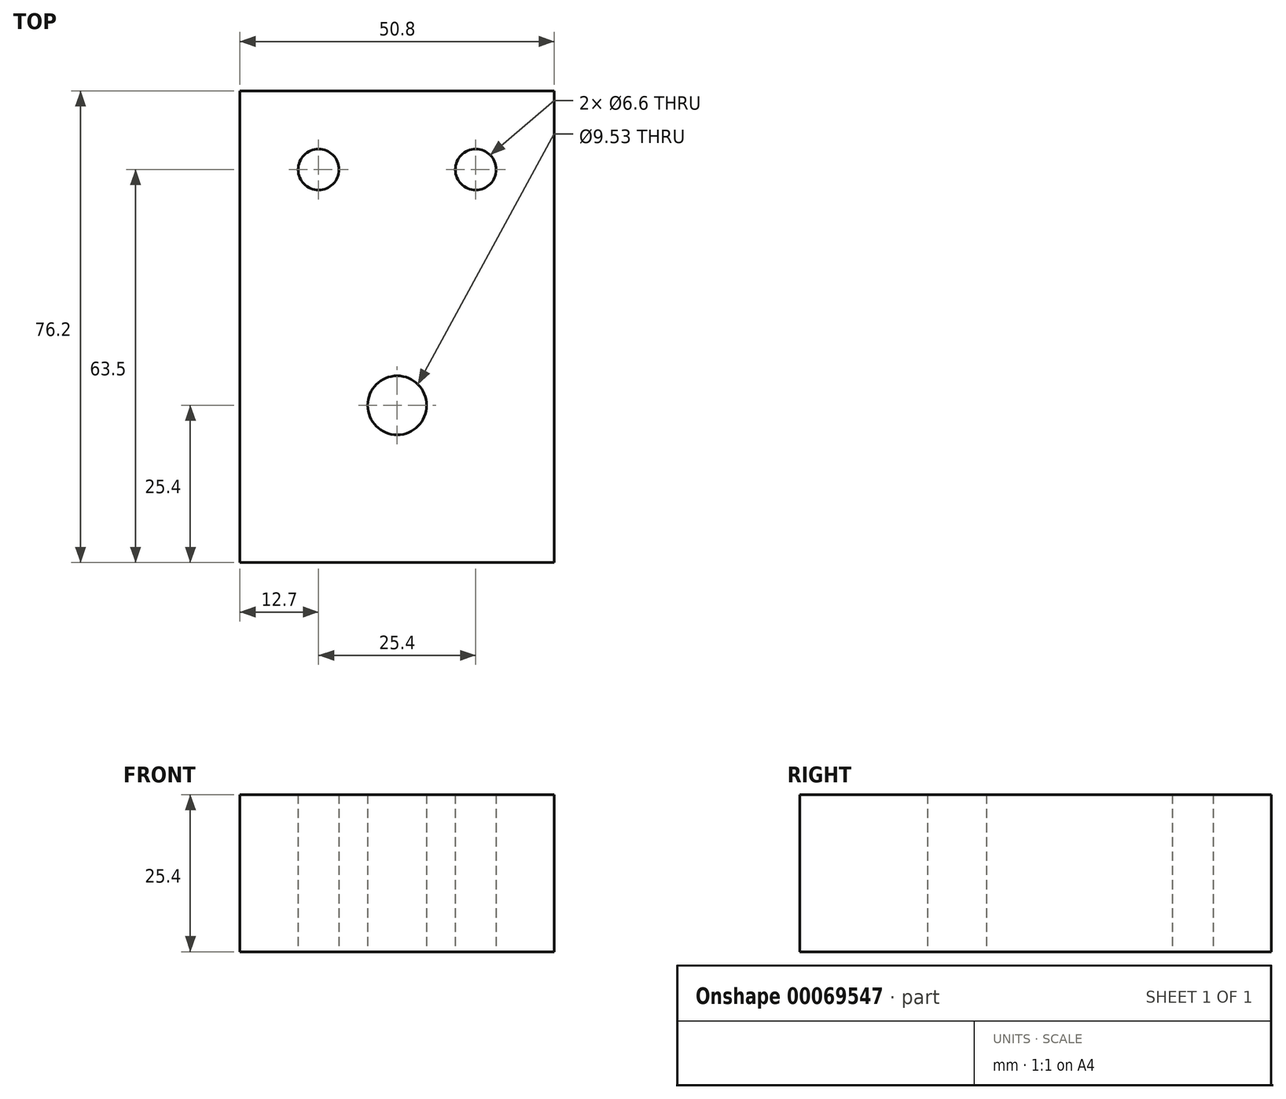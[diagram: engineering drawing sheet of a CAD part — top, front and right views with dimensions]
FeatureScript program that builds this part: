
annotation { "Feature Type Name" : "Feature", "Feature Type Description" : "" }
export const myFeature = defineFeature(function(context is Context, id is Id, definition is map)
    precondition{}
    {
        {
            var Q0;
            Q0=qCreatedBy(makeId("Top.planeOp"),FACE);
            var sketch = newSketch(context, id + "F0", { "sketchPlane" : qUnion([Q0])});
            skLineSegment(sketch, "E0.rect.bottom", {"start": v(25.4, 38.1) * mm, "end": v(-25.4, 38.1) * mm});
            skLineSegment(sketch, "E0.rect.top", {"start": v(25.4, -38.1) * mm, "end": v(-25.4, -38.1) * mm});
            skLineSegment(sketch, "E0.rect.left", {"start": v(25.4, 38.1) * mm, "end": v(25.4, -38.1) * mm});
            skLineSegment(sketch, "E0.rect.right", {"start": v(-25.4, 38.1) * mm, "end": v(-25.4, -38.1) * mm});
            skPoint(sketch, "E0.rect.middle", {"position": v(0, 0) * mm});
            skCircle(sketch, "E1", {"center": v(12.7, 25.4) * mm, "radius": 3.3 * mm});
            skCircle(sketch, "E2", {"center": v(-12.7, 25.4) * mm, "radius": 3.3 * mm});
            skLineSegment(sketch, "E3", {"start": v(0, 38.1) * mm, "end": v(0, -38.1) * mm, "construction": true});
            skCircle(sketch, "E4", {"center": v(0, -12.7) * mm, "radius": 4.76 * mm});
            skSolve(sketch);
        }
        {
            var Q0;
            Q0=makeQuery(id+"F0.imprint","IMPRINT",FACE,{"disambiguationData":[TD([[makeQuery(id+"F0.imprint","IMPRINT",EDGE,{"derivedFrom":sQuery(id+"F0.wireOp",EDGE,"E0.rect.bottom")}),1.0]])]});
            extrude(context, id + "F1", {"entities" : qUnion([Q0]), "depth" : 25.4 * mm});
        }
    });
